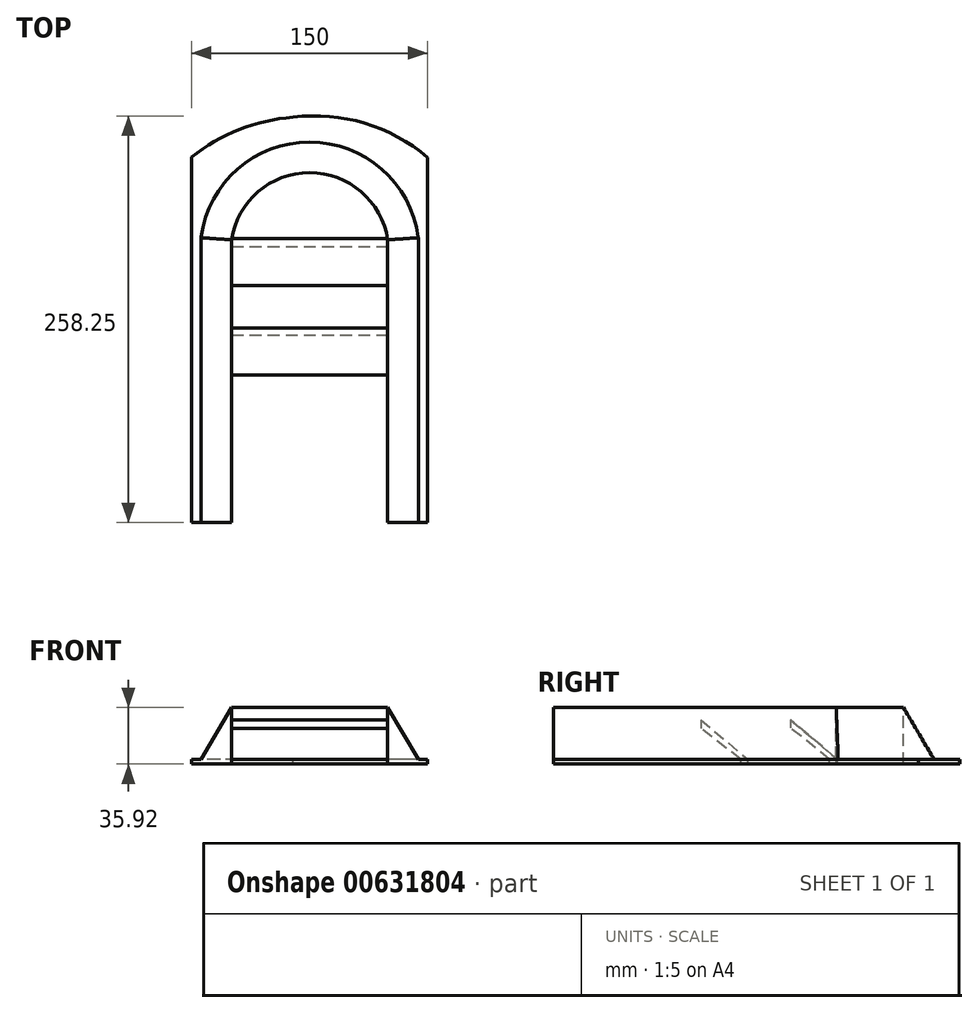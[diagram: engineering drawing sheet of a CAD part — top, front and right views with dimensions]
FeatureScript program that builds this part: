
annotation { "Feature Type Name" : "Feature", "Feature Type Description" : "" }
export const myFeature = defineFeature(function(context is Context, id is Id, definition is map)
    precondition{}
    {
        {
            var Q0;
            Q0=qCreatedBy(makeId("Front.planeOp"),FACE);
            var sketch = newSketch(context, id + "F0", { "sketchPlane" : qUnion([Q0])});
            skLineSegment(sketch, "E0.bottom", {"start": v(-62.08, 11.23) * mm, "end": v(87.92, 11.23) * mm});
            skLineSegment(sketch, "E0.top", {"start": v(-62.08, 8.23) * mm, "end": v(87.92, 8.23) * mm});
            skLineSegment(sketch, "E0.left", {"start": v(-62.08, 11.23) * mm, "end": v(-62.08, 8.23) * mm});
            skLineSegment(sketch, "E0.right", {"start": v(87.92, 11.23) * mm, "end": v(87.92, 8.23) * mm});
            skSolve(sketch);
        }
        {
            var Q0;
            Q0 = qSketchRegion(id + "F0", true);
            extrude(context, id + "F1", {"entities" : qUnion([Q0]), "depth" : 300 * mm, "offsetDistance" : 25 * mm});
        }
        {
            var Q0;
            Q0=makeQuery(id+"F1.opExtrude","SWEPT_FACE",FACE,{"disambiguationData":[OSD([sQuery(id+"F0.wireOp",EDGE,"E0.bottom")])]});
            var sketch = newSketch(context, id + "F2", { "sketchPlane" : qUnion([Q0])});
            skLineSegment(sketch, "E1.bottom", {"start": v(-37.4, -176.5) * mm, "end": v(62.6, -176.5) * mm});
            skLineSegment(sketch, "E1.top", {"start": v(-37.4, -206.5) * mm, "end": v(62.6, -206.5) * mm});
            skLineSegment(sketch, "E1.left", {"start": v(-37.4, -176.5) * mm, "end": v(-37.4, -206.5) * mm});
            skLineSegment(sketch, "E1.right", {"start": v(62.6, -176.5) * mm, "end": v(62.6, -206.5) * mm});
            skSolve(sketch);
        }
        {
            var Q0;
            Q0 = qSketchRegion(id + "F2", true);
            extrude(context, id + "F3", {"entities" : qUnion([Q0]), "operationType" : NewBodyOperationType.ADD, "depth" : 25 * mm, "offsetDistance" : 25 * mm});
        }
        {
            var Q0;
            Q0=makeQuery(id+"F3.opExtrude","SWEPT_FACE",FACE,{"disambiguationData":[OSD([sQuery(id+"F2.wireOp",EDGE,"E1.right")])]});
            var sketch = newSketch(context, id + "F4", { "sketchPlane" : qUnion([Q0])});
            skLineSegment(sketch, "E2", {"start": v(-206.5, 30.87) * mm, "end": v(-206.5, 36.23) * mm});
            skLineSegment(sketch, "E3", {"start": v(-206.5, 36.23) * mm, "end": v(-176.5, 11.23) * mm});
            skLineSegment(sketch, "E4", {"start": v(-176.5, 11.23) * mm, "end": v(-181.07, 11.23) * mm});
            skLineSegment(sketch, "E5", {"start": v(-181.07, 11.23) * mm, "end": v(-206.5, 30.87) * mm});
            skSolve(sketch);
        }
        {
            var Q0;
            Q0=makeQuery(id+"F4.imprint","IMPRINT",FACE,{"disambiguationData":[TD([[makeQuery(id+"F4.imprint","IMPRINT",EDGE,{"derivedFrom":sQuery(id+"F4.wireOp",EDGE,"E3")}),1.0]])]});
            var Q1;
            {var subQ0=sQuery(id+"F4.wireOp",EDGE,"E5");Q1=makeQuery(id+"F4.imprint","IMPRINT",FACE,{"disambiguationData":[TD([[makeQuery(id+"F4.imprint","IMPRINT",EDGE,{"derivedFrom":subQ0}),1.0]])]});}
            extrude(context, id + "F5", {"entities" : qUnion([Q0, Q1]), "operationType" : NewBodyOperationType.REMOVE, "oppositeDirection" : true, "depth" : 100 * mm, "offsetDistance" : 25 * mm});
        }
        {
            var Q0;
            {var subQ0=sQuery(id+"F2.wireOp",EDGE,"E1.right");var subQ1=makeQuery(id+"F3.opExtrude","CAP_EDGE",EDGE,{"disambiguationData":[OSD([subQ0])],"isStart":true});Q0=makeQuery(id+"F5.boolean.opBoolean","MERGE",FACE,{"derivedFrom":[makeQuery(id+"F1.opExtrude","SWEPT_FACE",FACE,{"disambiguationData":[OSD([sQuery(id+"F0.wireOp",EDGE,"E0.bottom")])]}),makeQuery(id+"F5.opExtrude","SWEPT_FACE",FACE,{"disambiguationData":[OSD([subQ0]),TDD([makeQuery(id+"F4.imprint","IMPRINT",EDGE,{"disambiguationData":[TD([[makeQuery(id+"F4.imprint","INTERSECT",VERTEX,{"derivedFrom":[makeQuery(id+"F3.opExtrude","SWEPT_EDGE",EDGE,{"disambiguationData":[OSD([sQuery(id+"F2.wireOp",EDGE,"E1.top"),subQ0])]}),subQ1]}),1.0]])],"derivedFrom":subQ1})])]})]});}
            var sketch = newSketch(context, id + "F6", { "sketchPlane" : qUnion([Q0])});
            skLineSegment(sketch, "E6.bottom", {"start": v(-37.4, -149.62) * mm, "end": v(62.6, -149.62) * mm});
            skLineSegment(sketch, "E6.top", {"start": v(-37.4, -119.62) * mm, "end": v(62.6, -119.62) * mm});
            skLineSegment(sketch, "E6.left", {"start": v(-37.4, -149.62) * mm, "end": v(-37.4, -119.62) * mm});
            skLineSegment(sketch, "E6.right", {"start": v(62.6, -149.62) * mm, "end": v(62.6, -119.62) * mm});
            skSolve(sketch);
        }
        {
            var Q0;
            Q0 = qSketchRegion(id + "F6", true);
            extrude(context, id + "F7", {"entities" : qUnion([Q0]), "operationType" : NewBodyOperationType.ADD, "depth" : 25 * mm, "offsetDistance" : 25 * mm});
        }
        {
            var Q0;
            Q0=makeQuery(id+"F7.opExtrude","SWEPT_FACE",FACE,{"disambiguationData":[OSD([sQuery(id+"F6.wireOp",EDGE,"E6.right")])]});
            var sketch = newSketch(context, id + "F8", { "sketchPlane" : qUnion([Q0])});
            skLineSegment(sketch, "E7", {"start": v(-149.62, 31.28) * mm, "end": v(-149.62, 36.23) * mm});
            skLineSegment(sketch, "E8", {"start": v(-149.62, 36.23) * mm, "end": v(-119.62, 11.23) * mm});
            skLineSegment(sketch, "E9", {"start": v(-119.62, 11.23) * mm, "end": v(-124.67, 11.23) * mm});
            skLineSegment(sketch, "E10", {"start": v(-124.67, 11.23) * mm, "end": v(-149.62, 31.28) * mm});
            skSolve(sketch);
        }
        {
            var Q0;
            Q0=makeQuery(id+"F8.imprint","IMPRINT",FACE,{"disambiguationData":[TD([[makeQuery(id+"F8.imprint","IMPRINT",EDGE,{"derivedFrom":sQuery(id+"F8.wireOp",EDGE,"E8")}),1.0]])]});
            var Q1;
            {var subQ0=sQuery(id+"F8.wireOp",EDGE,"E10");Q1=makeQuery(id+"F8.imprint","IMPRINT",FACE,{"disambiguationData":[TD([[makeQuery(id+"F8.imprint","IMPRINT",EDGE,{"derivedFrom":subQ0}),1.0]])]});}
            extrude(context, id + "F9", {"entities" : qUnion([Q0, Q1]), "operationType" : NewBodyOperationType.REMOVE, "oppositeDirection" : true, "depth" : 100 * mm, "offsetDistance" : 25 * mm});
        }
        {
            var Q0;
            {var subQ0=sQuery(id+"F6.wireOp",EDGE,"E6.right");var subQ1=makeQuery(id+"F7.opExtrude","CAP_EDGE",EDGE,{"disambiguationData":[OSD([subQ0])],"isStart":true});var subQ2=sQuery(id+"F2.wireOp",EDGE,"E1.right");var subQ3=makeQuery(id+"F3.opExtrude","CAP_EDGE",EDGE,{"disambiguationData":[OSD([subQ2])],"isStart":true});Q0=makeQuery(id+"F9.boolean.opBoolean","MERGE",FACE,{"derivedFrom":[makeQuery(id+"F5.boolean.opBoolean","MERGE",FACE,{"derivedFrom":[makeQuery(id+"F1.opExtrude","SWEPT_FACE",FACE,{"disambiguationData":[OSD([sQuery(id+"F0.wireOp",EDGE,"E0.bottom")])]}),makeQuery(id+"F5.opExtrude","SWEPT_FACE",FACE,{"disambiguationData":[OSD([subQ2]),TDD([makeQuery(id+"F4.imprint","IMPRINT",EDGE,{"disambiguationData":[TD([[makeQuery(id+"F4.imprint","INTERSECT",VERTEX,{"derivedFrom":[makeQuery(id+"F3.opExtrude","SWEPT_EDGE",EDGE,{"disambiguationData":[OSD([sQuery(id+"F2.wireOp",EDGE,"E1.top"),subQ2])]}),subQ3]}),1.0]])],"derivedFrom":subQ3})])]})]}),makeQuery(id+"F9.opExtrude","SWEPT_FACE",FACE,{"disambiguationData":[OSD([subQ0]),TDD([makeQuery(id+"F8.imprint","IMPRINT",EDGE,{"disambiguationData":[TD([[makeQuery(id+"F8.imprint","INTERSECT",VERTEX,{"derivedFrom":[makeQuery(id+"F7.opExtrude","SWEPT_EDGE",EDGE,{"disambiguationData":[OSD([sQuery(id+"F6.wireOp",EDGE,"E6.bottom"),subQ0])]}),subQ1]}),-1.0]])],"derivedFrom":subQ1})])]})]});}
            var sketch = newSketch(context, id + "F10", { "sketchPlane" : qUnion([Q0])});
            skLineSegment(sketch, "E11", {"start": v(74.85, -300) * mm, "end": v(74.85, -119.62) * mm});
            skLineSegment(sketch, "E12", {"start": v(-48.77, -300) * mm, "end": v(-48.77, -119.62) * mm});
            skArc(sketch, "E13", {"start": v(74.85, -119.62) * mm, "mid": v(13.04, -65.54) * mm, "end": v(-48.77, -119.62) * mm});
            skSolve(sketch);
        }
        {
            var Q0;
            Q0=makeQuery(id+"F1.opExtrude","CAP_FACE",FACE,{"disambiguationData":[OSD([sQuery(id+"F0.wireOp",EDGE,"E0.bottom"),sQuery(id+"F0.wireOp",EDGE,"E0.top"),sQuery(id+"F0.wireOp",EDGE,"E0.left"),sQuery(id+"F0.wireOp",EDGE,"E0.right")])],"isStart":false});
            var sketch = newSketch(context, id + "F11", { "sketchPlane" : qUnion([Q0])});
            skLineSegment(sketch, "E14", {"start": v(62.62, 11.23) * mm, "end": v(62.62, 44.15) * mm});
            skLineSegment(sketch, "E15", {"start": v(62.62, 44.15) * mm, "end": v(82.06, 11.23) * mm});
            skLineSegment(sketch, "E16", {"start": v(82.06, 11.23) * mm, "end": v(62.62, 11.23) * mm});
            skSolve(sketch);
        }
        {
            var Q0;
            Q0=makeQuery(id+"F11.imprint","IMPRINT",FACE,{"disambiguationData":[TD([[makeQuery(id+"F11.imprint","IMPRINT",EDGE,{"derivedFrom":sQuery(id+"F11.wireOp",EDGE,"E14")}),-1.0]])]});
            var Q1;
            Q1=sQuery(id+"F10.wireOp",EDGE,"E11");
            var Q2;
            Q2=sQuery(id+"F10.wireOp",EDGE,"E13");
            var Q3;
            Q3=sQuery(id+"F10.wireOp",EDGE,"E12");
            sweep(context, id + "F12", {"operationType" : NewBodyOperationType.ADD, "profiles" : qUnion([Q0]), "path" : qUnion([Q1, Q2, Q3])});
        }
        {
            var Q0;
            {var subQ0=sQuery(id+"F6.wireOp",EDGE,"E6.right");var subQ1=makeQuery(id+"F7.opExtrude","CAP_EDGE",EDGE,{"disambiguationData":[OSD([subQ0])],"isStart":true});var subQ2=sQuery(id+"F2.wireOp",EDGE,"E1.right");var subQ3=makeQuery(id+"F3.opExtrude","CAP_EDGE",EDGE,{"disambiguationData":[OSD([subQ2])],"isStart":true});Q0=makeQuery(id+"F12.boolean.opBoolean","SPLIT",FACE,{"disambiguationData":[TD([makeQuery(id+"F9.boolean.opBoolean","COPY",FACE,{"derivedFrom":makeQuery(id+"F9.opExtrude","SWEPT_FACE",FACE,{"disambiguationData":[OSD([sQuery(id+"F8.wireOp",EDGE,"E8")])]})})])],"derivedFrom":makeQuery(id+"F9.boolean.opBoolean","MERGE",FACE,{"derivedFrom":[makeQuery(id+"F5.boolean.opBoolean","MERGE",FACE,{"derivedFrom":[makeQuery(id+"F1.opExtrude","SWEPT_FACE",FACE,{"disambiguationData":[OSD([sQuery(id+"F0.wireOp",EDGE,"E0.bottom")])]}),makeQuery(id+"F5.opExtrude","SWEPT_FACE",FACE,{"disambiguationData":[OSD([subQ2]),TDD([makeQuery(id+"F4.imprint","IMPRINT",EDGE,{"disambiguationData":[TD([[makeQuery(id+"F4.imprint","INTERSECT",VERTEX,{"derivedFrom":[makeQuery(id+"F3.opExtrude","SWEPT_EDGE",EDGE,{"disambiguationData":[OSD([sQuery(id+"F2.wireOp",EDGE,"E1.top"),subQ2])]}),subQ3]}),1.0]])],"derivedFrom":subQ3})])]})]}),makeQuery(id+"F9.opExtrude","SWEPT_FACE",FACE,{"disambiguationData":[OSD([subQ0]),TDD([makeQuery(id+"F8.imprint","IMPRINT",EDGE,{"disambiguationData":[TD([[makeQuery(id+"F8.imprint","INTERSECT",VERTEX,{"derivedFrom":[makeQuery(id+"F7.opExtrude","SWEPT_EDGE",EDGE,{"disambiguationData":[OSD([sQuery(id+"F6.wireOp",EDGE,"E6.bottom"),subQ0])]}),subQ1]}),-1.0]])],"derivedFrom":subQ1})])]})]})});}
            extrude(context, id + "F13", {"entities" : qUnion([Q0]), "operationType" : NewBodyOperationType.REMOVE, "oppositeDirection" : true, "depth" : 25 * mm, "offsetDistance" : 25 * mm});
        }
        {
            var Q0;
            {var subQ5=sQuery(id+"F6.wireOp",EDGE,"E6.right");var subQ6=sQuery(id+"F0.wireOp",EDGE,"E0.bottom");var subQ7=sQuery(id+"F2.wireOp",EDGE,"E1.right");var subQ8=makeQuery(id+"F7.opExtrude","CAP_EDGE",EDGE,{"disambiguationData":[OSD([subQ5])],"isStart":true});var subQ9=makeQuery(id+"F3.opExtrude","CAP_EDGE",EDGE,{"disambiguationData":[OSD([subQ7])],"isStart":true});Q0=makeQuery(id+"F12.boolean.opBoolean","SPLIT",FACE,{"disambiguationData":[TD([makeQuery(id+"F3.opExtrude","SWEPT_FACE",FACE,{"disambiguationData":[OSD([subQ7])]})])],"derivedFrom":makeQuery(id+"F9.boolean.opBoolean","MERGE",FACE,{"derivedFrom":[makeQuery(id+"F5.boolean.opBoolean","MERGE",FACE,{"derivedFrom":[makeQuery(id+"F1.opExtrude","SWEPT_FACE",FACE,{"disambiguationData":[OSD([subQ6])]}),makeQuery(id+"F5.opExtrude","SWEPT_FACE",FACE,{"disambiguationData":[OSD([subQ7]),TDD([makeQuery(id+"F4.imprint","IMPRINT",EDGE,{"disambiguationData":[TD([[makeQuery(id+"F4.imprint","INTERSECT",VERTEX,{"derivedFrom":[makeQuery(id+"F3.opExtrude","SWEPT_EDGE",EDGE,{"disambiguationData":[OSD([sQuery(id+"F2.wireOp",EDGE,"E1.top"),subQ7])]}),subQ9]}),1.0]])],"derivedFrom":subQ9})])]})]}),makeQuery(id+"F9.opExtrude","SWEPT_FACE",FACE,{"disambiguationData":[OSD([subQ5]),TDD([makeQuery(id+"F8.imprint","IMPRINT",EDGE,{"disambiguationData":[TD([[makeQuery(id+"F8.imprint","INTERSECT",VERTEX,{"derivedFrom":[makeQuery(id+"F7.opExtrude","SWEPT_EDGE",EDGE,{"disambiguationData":[OSD([sQuery(id+"F6.wireOp",EDGE,"E6.bottom"),subQ5])]}),subQ8]}),-1.0]])],"derivedFrom":subQ8})])]})]})});}
            extrude(context, id + "F14", {"entities" : qUnion([Q0]), "operationType" : NewBodyOperationType.REMOVE, "oppositeDirection" : true, "depth" : 25 * mm, "offsetDistance" : 25 * mm});
        }
        {
            var Q0;
            {var subQ4=sQuery(id+"F0.wireOp",EDGE,"E0.left");var subQ6=sQuery(id+"F0.wireOp",EDGE,"E0.bottom");var subQ7=sQuery(id+"F6.wireOp",EDGE,"E6.right");var subQ8=makeQuery(id+"F7.opExtrude","CAP_EDGE",EDGE,{"disambiguationData":[OSD([subQ7])],"isStart":true});var subQ9=sQuery(id+"F2.wireOp",EDGE,"E1.right");var subQ10=makeQuery(id+"F3.opExtrude","CAP_EDGE",EDGE,{"disambiguationData":[OSD([subQ9])],"isStart":true});Q0=makeQuery(id+"F12.boolean.opBoolean","SPLIT",FACE,{"disambiguationData":[TD([makeQuery(id+"F1.opExtrude","SWEPT_FACE",FACE,{"disambiguationData":[OSD([subQ4])]})])],"derivedFrom":makeQuery(id+"F9.boolean.opBoolean","MERGE",FACE,{"derivedFrom":[makeQuery(id+"F5.boolean.opBoolean","MERGE",FACE,{"derivedFrom":[makeQuery(id+"F1.opExtrude","SWEPT_FACE",FACE,{"disambiguationData":[OSD([subQ6])]}),makeQuery(id+"F5.opExtrude","SWEPT_FACE",FACE,{"disambiguationData":[OSD([subQ9]),TDD([makeQuery(id+"F4.imprint","IMPRINT",EDGE,{"disambiguationData":[TD([[makeQuery(id+"F4.imprint","INTERSECT",VERTEX,{"derivedFrom":[makeQuery(id+"F3.opExtrude","SWEPT_EDGE",EDGE,{"disambiguationData":[OSD([sQuery(id+"F2.wireOp",EDGE,"E1.top"),subQ9])]}),subQ10]}),1.0]])],"derivedFrom":subQ10})])]})]}),makeQuery(id+"F9.opExtrude","SWEPT_FACE",FACE,{"disambiguationData":[OSD([subQ7]),TDD([makeQuery(id+"F8.imprint","IMPRINT",EDGE,{"disambiguationData":[TD([[makeQuery(id+"F8.imprint","INTERSECT",VERTEX,{"derivedFrom":[makeQuery(id+"F7.opExtrude","SWEPT_EDGE",EDGE,{"disambiguationData":[OSD([sQuery(id+"F6.wireOp",EDGE,"E6.bottom"),subQ7])]}),subQ8]}),-1.0]])],"derivedFrom":subQ8})])]})]})});}
            var sketch = newSketch(context, id + "F15", { "sketchPlane" : qUnion([Q0])});
            skArc(sketch, "E17", {"start": v(87.92, -68.1) * mm, "mid": v(47.93, -46.38) * mm, "end": v(2.58, -42.6) * mm});
            skArc(sketch, "E18", {"start": v(2.58, -42.6) * mm, "mid": v(-31.68, -50.4) * mm, "end": v(-62.08, -68.01) * mm});
            skSolve(sketch);
        }
        {
            var Q0;
            {var subQ4=sQuery(id+"F15.wireOp",EDGE,"E17");Q0=makeQuery(id+"F15.imprint","IMPRINT",FACE,{"disambiguationData":[TD([[makeQuery(id+"F15.imprint","IMPRINT",EDGE,{"derivedFrom":subQ4}),-1.0]])]});}
            extrude(context, id + "F16", {"entities" : qUnion([Q0]), "operationType" : NewBodyOperationType.REMOVE, "oppositeDirection" : true, "depth" : 25 * mm, "offsetDistance" : 25 * mm});
        }
    });
